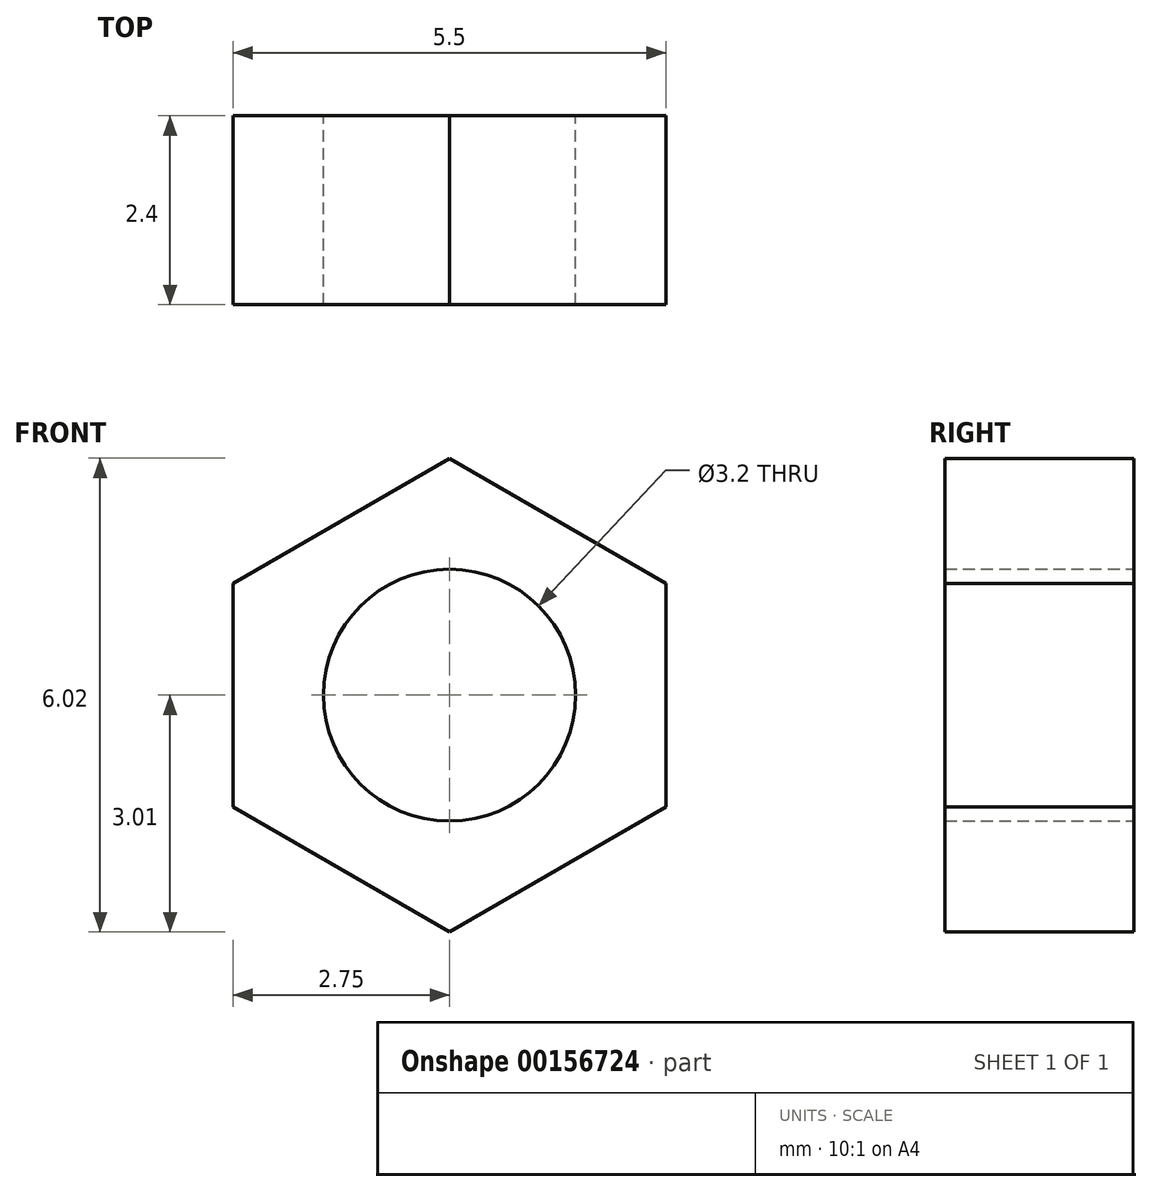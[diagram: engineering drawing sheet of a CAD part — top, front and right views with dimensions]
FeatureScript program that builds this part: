
annotation { "Feature Type Name" : "Feature", "Feature Type Description" : "" }
export const myFeature = defineFeature(function(context is Context, id is Id, definition is map)
    precondition{}
    {
        {
            var Q0;
            Q0=qCreatedBy(makeId("Front.planeOp"),FACE);
            var sketch = newSketch(context, id + "F0", { "sketchPlane" : qUnion([Q0])});
            skLineSegment(sketch, "E0", {"start": v(-2.75, 1.42) * mm, "end": v(-2.75, -1.42) * mm});
            skLineSegment(sketch, "E1", {"start": v(-2.75, -1.42) * mm, "end": v(0, -3) * mm});
            skLineSegment(sketch, "E2", {"start": v(0, -3) * mm, "end": v(2.75, -1.42) * mm});
            skLineSegment(sketch, "E3", {"start": v(2.75, -1.42) * mm, "end": v(2.75, 1.42) * mm});
            skLineSegment(sketch, "E4", {"start": v(2.75, 1.42) * mm, "end": v(0, 3) * mm});
            skLineSegment(sketch, "E5", {"start": v(0, 3) * mm, "end": v(-2.75, 1.42) * mm});
            skCircle(sketch, "E6", {"center": v(0, 0) * mm, "radius": 1.6 * mm});
            skSolve(sketch);
        }
        {
            var Q0;
            Q0=makeQuery(id+"F0.imprint","IMPRINT",FACE,{"disambiguationData":[TD([[makeQuery(id+"F0.imprint","IMPRINT",EDGE,{"derivedFrom":sQuery(id+"F0.wireOp",EDGE,"E0")}),1.0]])]});
            extrude(context, id + "F1", {"entities" : qUnion([Q0]), "depth" : 2.4 * mm});
        }
    });
